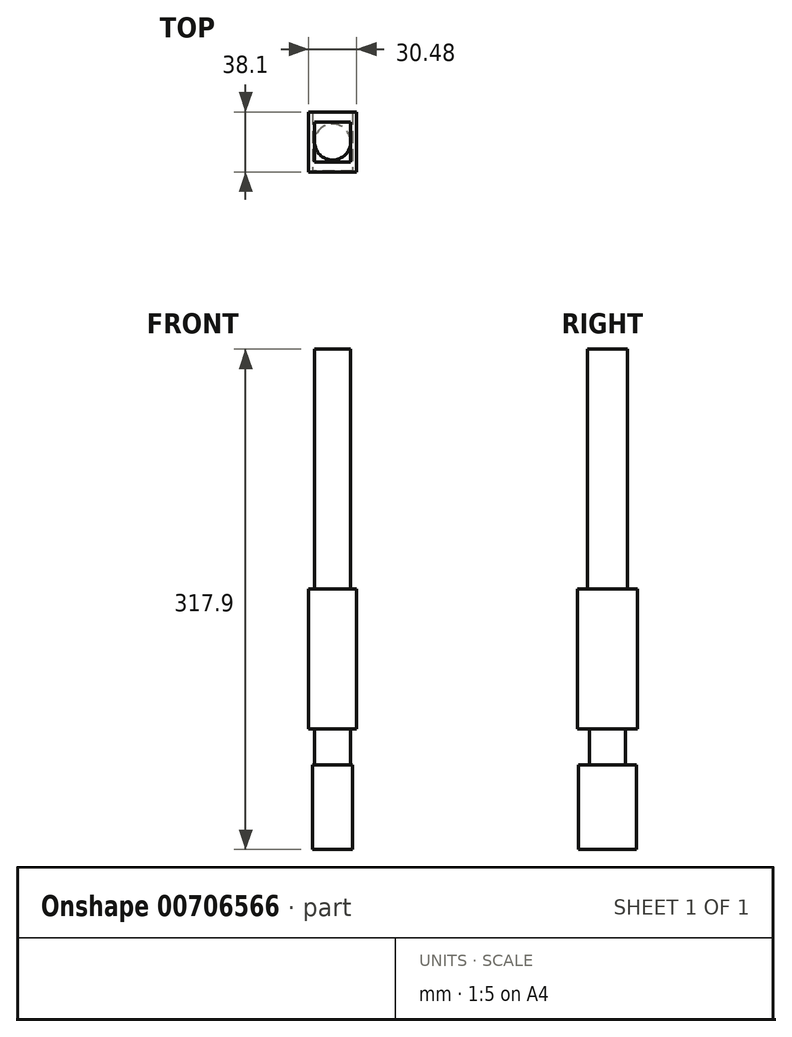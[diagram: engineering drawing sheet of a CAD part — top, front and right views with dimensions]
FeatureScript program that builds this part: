
annotation { "Feature Type Name" : "Feature", "Feature Type Description" : "" }
export const myFeature = defineFeature(function(context is Context, id is Id, definition is map)
    precondition{}
    {
        {
            var Q0;
            Q0=qCreatedBy(makeId("Top.planeOp"),FACE);
            var sketch = newSketch(context, id + "F0", { "sketchPlane" : qUnion([Q0])});
            skLineSegment(sketch, "E0.bottom", {"start": v(15.24, 19.05) * mm, "end": v(-15.24, 19.05) * mm});
            skLineSegment(sketch, "E0.top", {"start": v(15.24, -19.05) * mm, "end": v(-15.24, -19.05) * mm});
            skLineSegment(sketch, "E0.left", {"start": v(15.24, 19.05) * mm, "end": v(15.24, -19.05) * mm});
            skLineSegment(sketch, "E0.right", {"start": v(-15.24, 19.05) * mm, "end": v(-15.24, -19.05) * mm});
            skPoint(sketch, "E0.middle", {"position": v(0, 0) * mm});
            skSolve(sketch);
        }
        {
            var Q0;
            Q0 = qSketchRegion(id + "F0", true);
            var Q1;
            Q1=makeQuery(id+"F0.imprint","IMPRINT",FACE,{"disambiguationData":[TD([[makeQuery(id+"F0.imprint","IMPRINT",EDGE,{"derivedFrom":sQuery(id+"F0.wireOp",EDGE,"E0.bottom")}),1.0]])]});
            extrude(context, id + "F1", {"entities" : qUnion([Q0, Q1]), "depth" : 88.9 * mm, "offsetDistance" : 25.4 * mm});
        }
        {
            var Q0;
            Q0=makeQuery(id+"F1.opExtrude","CAP_FACE",FACE,{"disambiguationData":[OSD([sQuery(id+"F0.wireOp",EDGE,"E0.bottom"),sQuery(id+"F0.wireOp",EDGE,"E0.top"),sQuery(id+"F0.wireOp",EDGE,"E0.left"),sQuery(id+"F0.wireOp",EDGE,"E0.right")])],"isStart":false});
            var sketch = newSketch(context, id + "F2", { "sketchPlane" : qUnion([Q0])});
            skLineSegment(sketch, "E1.bottom", {"start": v(11.43, 12.7) * mm, "end": v(-11.43, 12.7) * mm});
            skLineSegment(sketch, "E1.top", {"start": v(11.43, -12.7) * mm, "end": v(-11.43, -12.7) * mm});
            skLineSegment(sketch, "E1.left", {"start": v(11.43, 12.7) * mm, "end": v(11.43, -12.7) * mm});
            skLineSegment(sketch, "E1.right", {"start": v(-11.43, 12.7) * mm, "end": v(-11.43, -12.7) * mm});
            skPoint(sketch, "E1.middle", {"position": v(0, 0) * mm});
            skSolve(sketch);
        }
        {
            var Q0;
            Q0=makeQuery(id+"F2.imprint","IMPRINT",FACE,{"disambiguationData":[TD([[makeQuery(id+"F2.imprint","IMPRINT",EDGE,{"derivedFrom":sQuery(id+"F2.wireOp",EDGE,"E1.bottom")}),1.0]])]});
            extrude(context, id + "F3", {"entities" : qUnion([Q0]), "operationType" : NewBodyOperationType.ADD, "depth" : 152.4 * mm, "offsetDistance" : 25.4 * mm});
        }
        {
            var Q0;
            Q0=makeQuery(id+"F1.opExtrude","CAP_FACE",FACE,{"disambiguationData":[OSD([sQuery(id+"F0.wireOp",EDGE,"E0.bottom"),sQuery(id+"F0.wireOp",EDGE,"E0.top"),sQuery(id+"F0.wireOp",EDGE,"E0.left"),sQuery(id+"F0.wireOp",EDGE,"E0.right")])],"isStart":true});
            var sketch = newSketch(context, id + "F4", { "sketchPlane" : qUnion([Q0])});
            skCircle(sketch, "E2", {"center": v(0, 0) * mm, "radius": 11.43 * mm});
            skSolve(sketch);
        }
        {
            var Q0;
            Q0 = qSketchRegion(id + "F4", true);
            extrude(context, id + "F5", {"entities" : qUnion([Q0]), "operationType" : NewBodyOperationType.ADD, "depth" : 22.86 * mm, "offsetDistance" : 25.4 * mm});
        }
        {
            var Q0;
            Q0=qCreatedBy(makeId("Right.planeOp"),FACE);
            var sketch = newSketch(context, id + "F6", { "sketchPlane" : qUnion([Q0])});
            skPoint(sketch, "E3.middle", {"position": v(0, 0) * mm});
            skLineSegment(sketch, "E4.bottom", {"start": v(-18.42, -76.6) * mm, "end": v(18.42, -76.6) * mm});
            skLineSegment(sketch, "E4.left", {"start": v(-18.42, -76.6) * mm, "end": v(-18.42, -22.86) * mm});
            skLineSegment(sketch, "E4.right", {"start": v(18.42, -76.6) * mm, "end": v(18.42, -22.86) * mm});
            skPoint(sketch, "E4.middle", {"position": v(0, -22.86) * mm});
            skPoint(sketch, "E5.end.orphan", {"position": v(11.43, -22.86) * mm});
            skPoint(sketch, "E6.trimOffspring.start.orphan", {"position": v(-11.43, -22.86) * mm});
            skLineSegment(sketch, "E7", {"start": v(18.42, -22.86) * mm, "end": v(-18.42, -22.86) * mm});
            skPoint(sketch, "E4.top.end.orphan", {"position": v(18.42, 30.88) * mm});
            skPoint(sketch, "E4.top.start.orphan", {"position": v(-18.42, 30.88) * mm});
            skPoint(sketch, "E3.top.end.orphan", {"position": v(11.43, 22.86) * mm});
            skPoint(sketch, "E3.top.start.orphan", {"position": v(-11.43, 22.86) * mm});
            skSolve(sketch);
        }
        {
            var Q0;
            Q0 = qSketchRegion(id + "F6", true);
            extrude(context, id + "F7", {"entities" : qUnion([Q0]), "operationType" : NewBodyOperationType.ADD, "depth" : 12.7 * mm, "offsetDistance" : 25.4 * mm});
        }
        {
            var Q0;
            Q0 = qSketchRegion(id + "F6", true);
            extrude(context, id + "F8", {"entities" : qUnion([Q0]), "operationType" : NewBodyOperationType.ADD, "oppositeDirection" : true, "depth" : 12.7 * mm, "offsetDistance" : 25.4 * mm});
        }
    });
